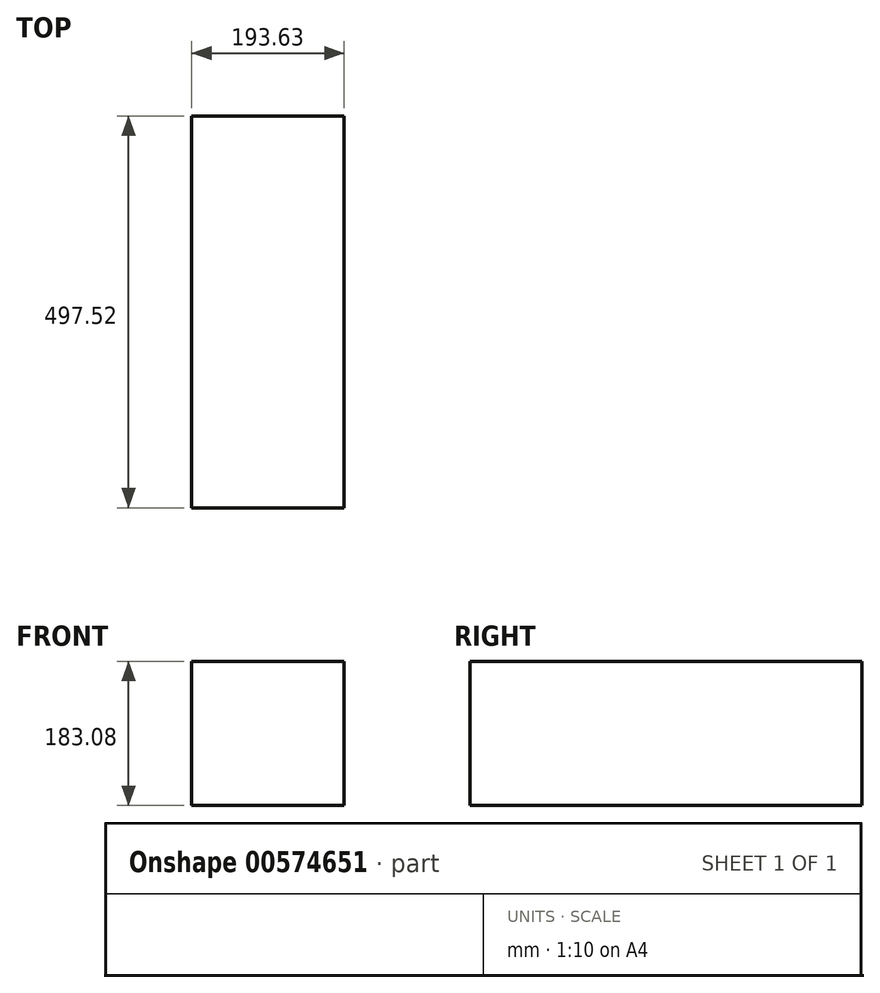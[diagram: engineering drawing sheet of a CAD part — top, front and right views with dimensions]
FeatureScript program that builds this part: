
annotation { "Feature Type Name" : "Feature", "Feature Type Description" : "" }
export const myFeature = defineFeature(function(context is Context, id is Id, definition is map)
    precondition{}
    {
        {
            var Q0;
            Q0=qCreatedBy(makeId("Front.planeOp"),FACE);
            var sketch = newSketch(context, id + "F0", { "sketchPlane" : qUnion([Q0])});
            skLineSegment(sketch, "E0.bottom", {"start": v(73, -78.03) * mm, "end": v(-120.64, -78.03) * mm});
            skLineSegment(sketch, "E0.top", {"start": v(73, 105.05) * mm, "end": v(-120.64, 105.05) * mm});
            skLineSegment(sketch, "E0.left", {"start": v(73, -78.03) * mm, "end": v(73, 105.05) * mm});
            skLineSegment(sketch, "E0.right", {"start": v(-120.64, -78.03) * mm, "end": v(-120.64, 105.05) * mm});
            skSolve(sketch);
        }
        {
            var Q0;
            Q0 = qSketchRegion(id + "F0", true);
            extrude(context, id + "F1", {"entities" : qUnion([Q0]), "depth" : 497.52 * mm, "offsetDistance" : 25.4 * mm});
        }
    });
